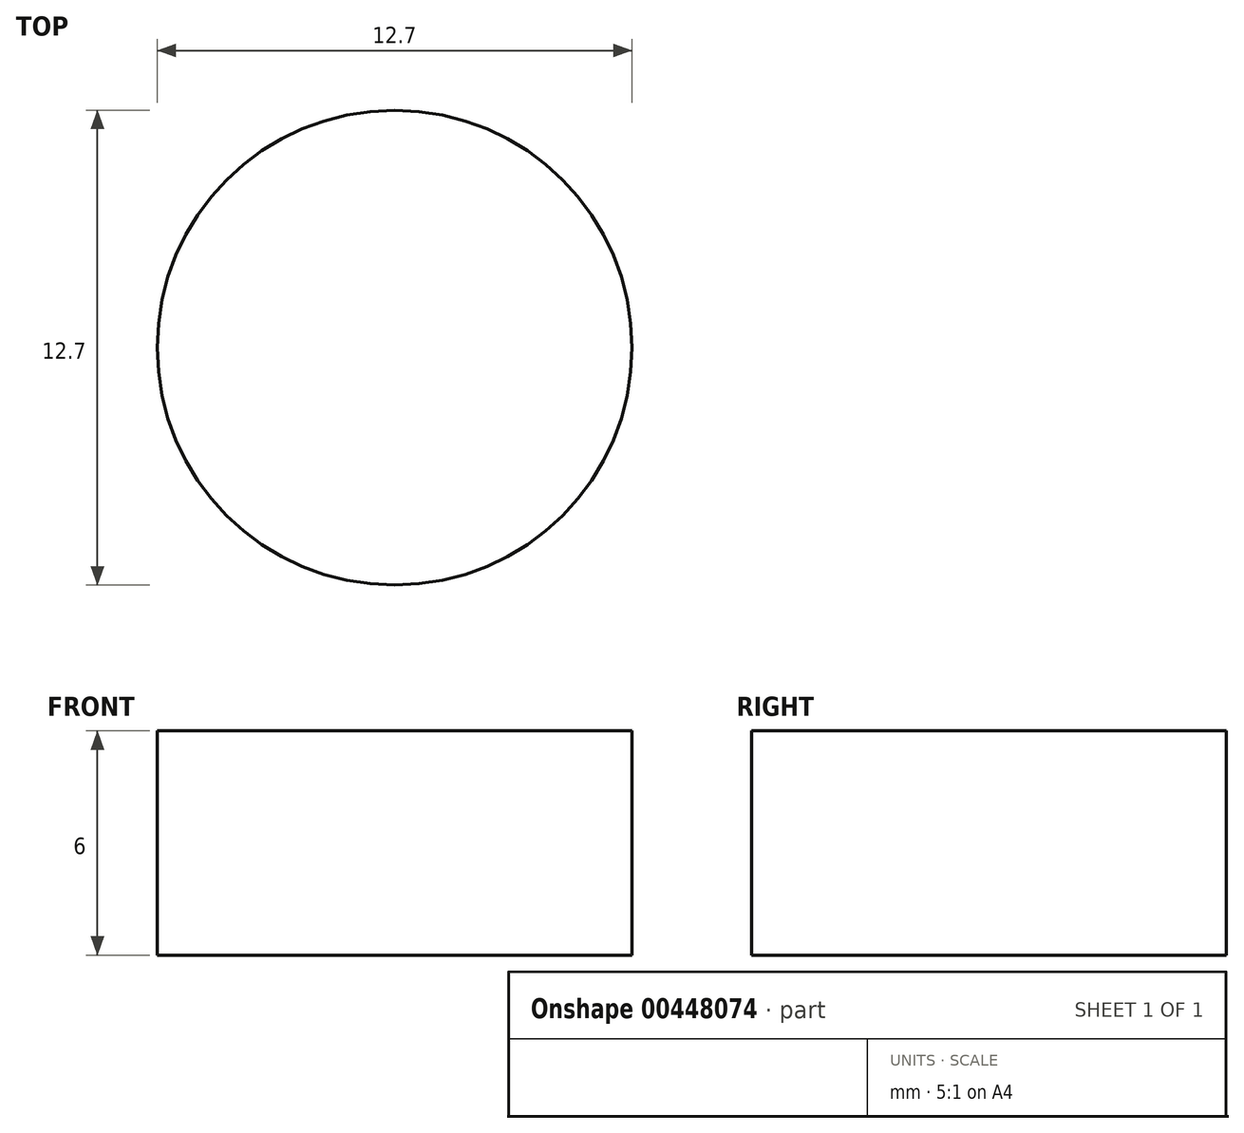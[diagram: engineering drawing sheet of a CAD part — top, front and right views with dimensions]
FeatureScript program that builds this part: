
annotation { "Feature Type Name" : "Feature", "Feature Type Description" : "" }
export const myFeature = defineFeature(function(context is Context, id is Id, definition is map)
    precondition{}
    {
        {
            assignVariable(context, id + "F0", {"name" : "ShaftL", "anyValue" : 6});
        }
        {
            var Q0;
            Q0=qCreatedBy(makeId("Top.planeOp"),FACE);
            var sketch = newSketch(context, id + "F1", { "sketchPlane" : qUnion([Q0])});
            skCircle(sketch, "E0", {"center": v(0, 0) * mm, "radius": 6.35 * mm});
            skSolve(sketch);
        }
        {
            var Q0;
            Q0=makeQuery(id+"F1.imprint","IMPRINT",FACE,{"disambiguationData":[TD([[makeQuery(id+"F1.imprint","IMPRINT",EDGE,{"derivedFrom":sQuery(id+"F1.wireOp",EDGE,"E0")}),1.0]])]});
            extrude(context, id + "F2", {"entities" : qUnion([Q0]), "depth" : (getVariable(context, 'ShaftL')) * mm});
        }
    });
